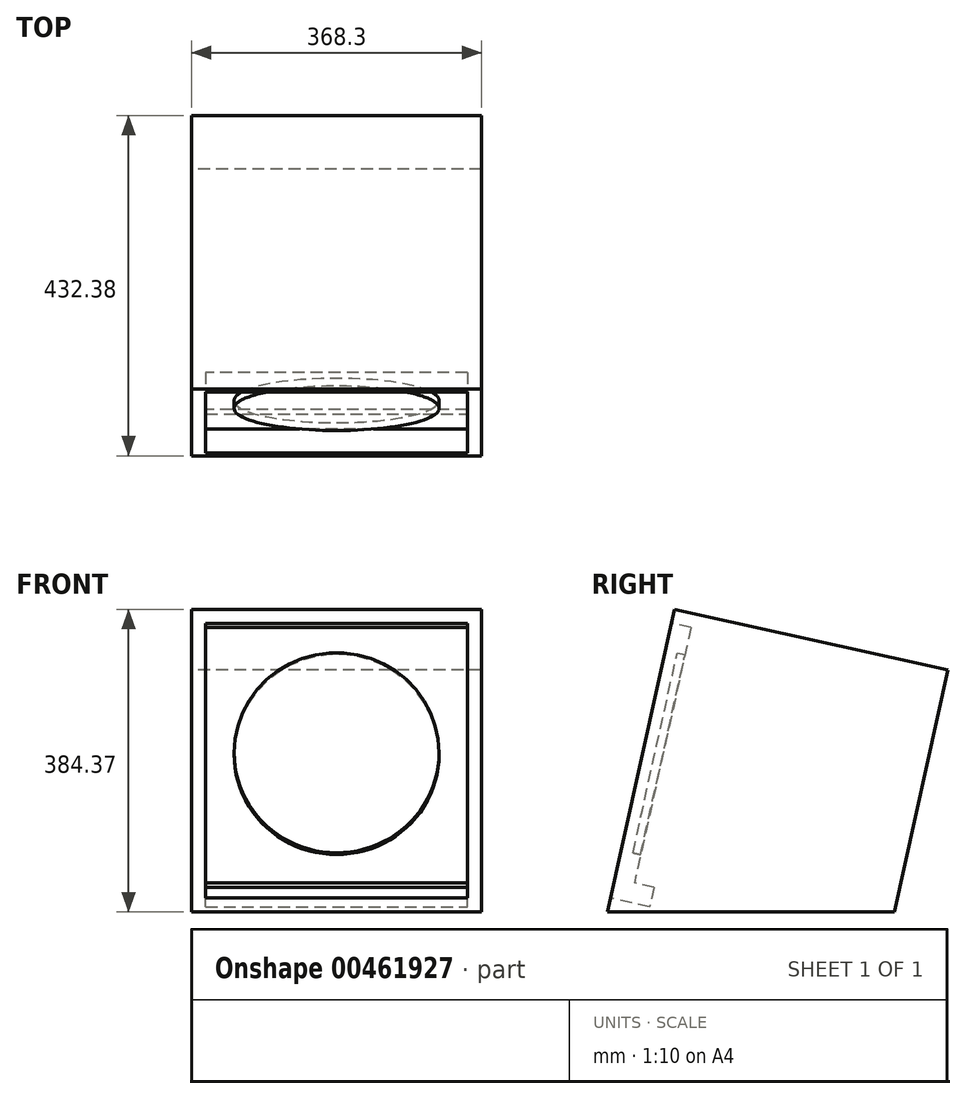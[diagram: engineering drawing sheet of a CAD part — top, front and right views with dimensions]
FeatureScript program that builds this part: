
annotation { "Feature Type Name" : "Feature", "Feature Type Description" : "" }
export const myFeature = defineFeature(function(context is Context, id is Id, definition is map)
    precondition{}
    {
        {
            var Q0;
            Q0=qCreatedBy(makeId("Right.planeOp"),FACE);
            var sketch = newSketch(context, id + "F0", { "sketchPlane" : qUnion([Q0])});
            skLineSegment(sketch, "E0", {"start": v(0, 0) * mm, "end": v(85.21, 384.37) * mm});
            skLineSegment(sketch, "E1", {"start": v(85.21, 384.37) * mm, "end": v(432.38, 307.4) * mm});
            skLineSegment(sketch, "E2", {"start": v(432.38, 307.4) * mm, "end": v(364.23, 0) * mm});
            skLineSegment(sketch, "E3", {"start": v(364.23, 0) * mm, "end": v(0, 0) * mm});
            skSolve(sketch);
        }
        {
            var Q0;
            Q0=makeQuery(id+"F0.imprint","IMPRINT",FACE,{"disambiguationData":[TD([[makeQuery(id+"F0.imprint","IMPRINT",EDGE,{"derivedFrom":sQuery(id+"F0.wireOp",EDGE,"E0")}),-1.0]])]});
            extrude(context, id + "F1", {"entities" : qUnion([Q0]), "depth" : 368.3 * mm});
        }
        {
            var Q0;
            Q0=makeQuery(id+"F1.opExtrude","SWEPT_FACE",FACE,{"disambiguationData":[OSD([sQuery(id+"F0.wireOp",EDGE,"E0")])]});
            var sketch = newSketch(context, id + "F2", { "sketchPlane" : qUnion([Q0])});
            skLineSegment(sketch, "E4", {"start": v(18.03, 375.67) * mm, "end": v(18.03, 18.03) * mm});
            skLineSegment(sketch, "E5", {"start": v(18.03, 18.03) * mm, "end": v(350.27, 18.03) * mm});
            skLineSegment(sketch, "E6", {"start": v(350.27, 18.03) * mm, "end": v(350.27, 375.67) * mm});
            skLineSegment(sketch, "E7", {"start": v(350.27, 375.67) * mm, "end": v(18.03, 375.67) * mm});
            skSolve(sketch);
        }
        {
            var Q0;
            Q0=makeQuery(id+"F2.imprint","IMPRINT",FACE,{"disambiguationData":[TD([[makeQuery(id+"F2.imprint","IMPRINT",EDGE,{"derivedFrom":sQuery(id+"F2.wireOp",EDGE,"E4")}),1.0]])]});
            extrude(context, id + "F3", {"entities" : qUnion([Q0]), "operationType" : NewBodyOperationType.REMOVE, "oppositeDirection" : true, "depth" : 25.4 * mm});
        }
        {
            var Q0;
            Q0=makeQuery(id+"F3.boolean.opBoolean","COPY",FACE,{"derivedFrom":makeQuery(id+"F3.opExtrude","CAP_FACE",FACE,{"disambiguationData":[OSD([sQuery(id+"F2.wireOp",EDGE,"E4"),sQuery(id+"F2.wireOp",EDGE,"E5"),sQuery(id+"F2.wireOp",EDGE,"E6"),sQuery(id+"F2.wireOp",EDGE,"E7")])],"isStart":false})});
            var sketch = newSketch(context, id + "F4", { "sketchPlane" : qUnion([Q0])});
            skCircle(sketch, "E8", {"center": v(184.15, 210.57) * mm, "radius": 130.18 * mm});
            skPoint(sketch, "E8.centerSnap0", {"position": v(184.15, 375.67) * mm});
            skSolve(sketch);
        }
        {
            var Q0;
            Q0=makeQuery(id+"F4.imprint","IMPRINT",FACE,{"disambiguationData":[TD([[makeQuery(id+"F4.imprint","IMPRINT",EDGE,{"derivedFrom":sQuery(id+"F4.wireOp",EDGE,"E8")}),1.0]])]});
            extrude(context, id + "F5", {"entities" : qUnion([Q0]), "operationType" : NewBodyOperationType.ADD, "depth" : 10.16 * mm});
        }
        {
            var Q0;
            Q0=makeQuery(id+"F3.boolean.opBoolean","COPY",FACE,{"derivedFrom":makeQuery(id+"F3.opExtrude","CAP_FACE",FACE,{"disambiguationData":[OSD([sQuery(id+"F2.wireOp",EDGE,"E4"),sQuery(id+"F2.wireOp",EDGE,"E5"),sQuery(id+"F2.wireOp",EDGE,"E6"),sQuery(id+"F2.wireOp",EDGE,"E7")])],"isStart":false})});
            var sketch = newSketch(context, id + "F6", { "sketchPlane" : qUnion([Q0])});
            skLineSegment(sketch, "E9", {"start": v(18.03, 18.03) * mm, "end": v(350.27, 18.03) * mm});
            skLineSegment(sketch, "E10", {"start": v(350.27, 18.03) * mm, "end": v(350.27, 43.43) * mm});
            skLineSegment(sketch, "E11", {"start": v(350.27, 43.43) * mm, "end": v(18.03, 43.43) * mm});
            skLineSegment(sketch, "E12", {"start": v(18.03, 43.43) * mm, "end": v(18.03, 18.03) * mm});
            skSolve(sketch);
        }
        {
            var Q0;
            Q0=makeQuery(id+"F6.imprint","IMPRINT",FACE,{"disambiguationData":[TD([[makeQuery(id+"F6.imprint","IMPRINT",EDGE,{"derivedFrom":sQuery(id+"F6.wireOp",EDGE,"E9")}),1.0]])]});
            extrude(context, id + "F7", {"entities" : qUnion([Q0]), "operationType" : NewBodyOperationType.REMOVE, "oppositeDirection" : true, "depth" : 25.4 * mm});
        }
    });
